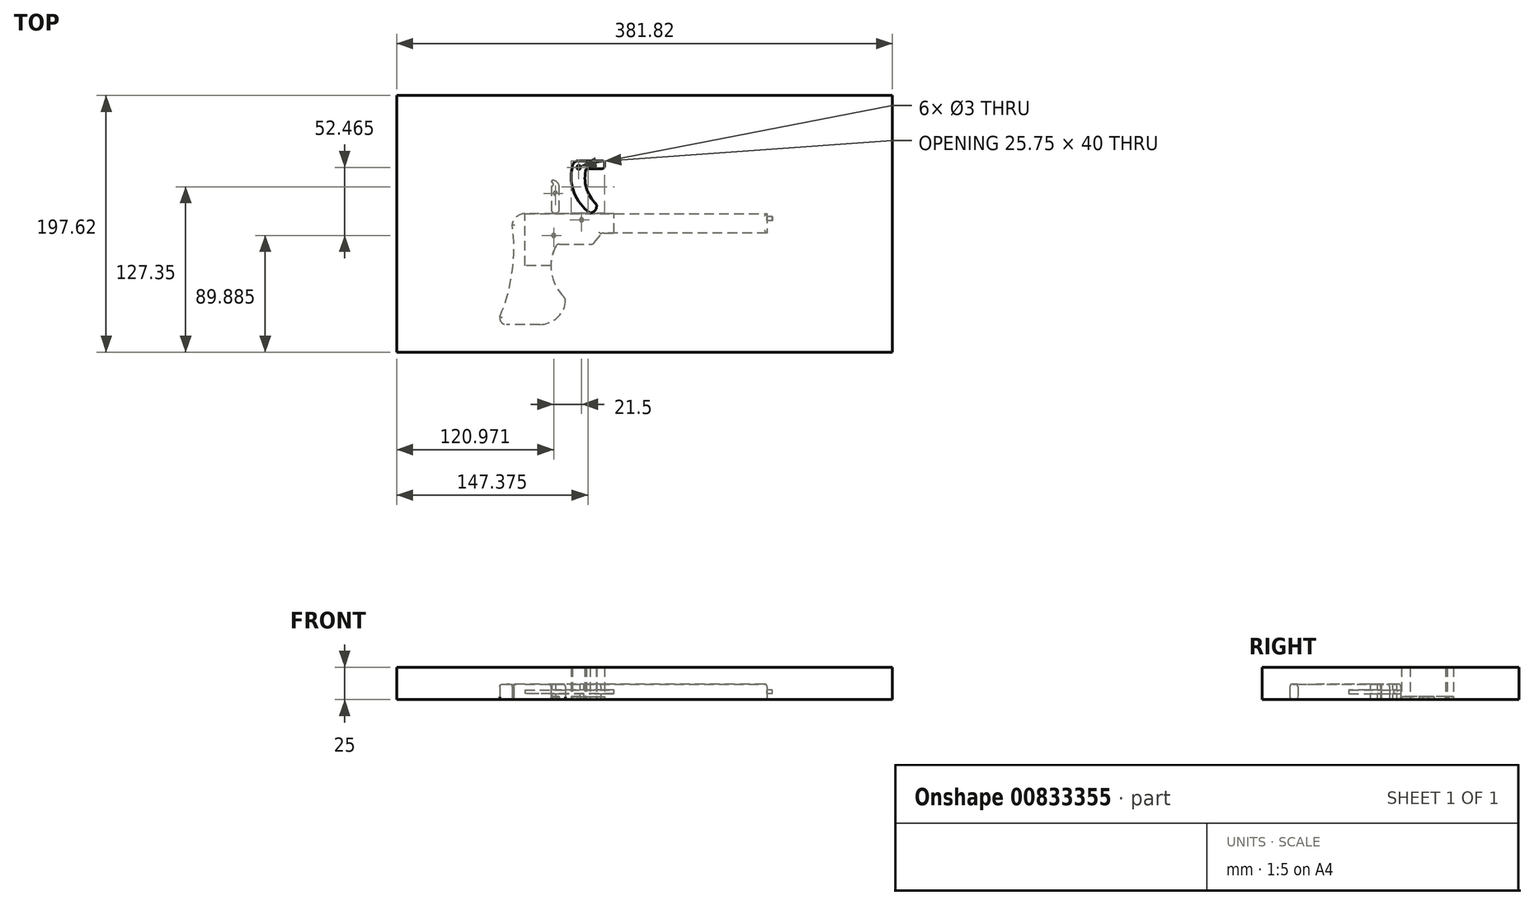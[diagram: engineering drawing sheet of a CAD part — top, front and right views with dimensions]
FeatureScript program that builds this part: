
annotation { "Feature Type Name" : "Feature", "Feature Type Description" : "" }
export const myFeature = defineFeature(function(context is Context, id is Id, definition is map)
    precondition{}
    {
        {
            var Q0;
            Q0=qCreatedBy(makeId("Top.planeOp"),FACE);
            var sketch = newSketch(context, id + "F0", { "sketchPlane" : qUnion([Q0])});
            skLineSegment(sketch, "E0", {"start": v(5, 40) * mm, "end": v(23, 40) * mm});
            skLineSegment(sketch, "E1", {"start": v(25, 38) * mm, "end": v(25, 36) * mm});
            skPoint(sketch, "E2.visualSharp", {"position": v(25, 40) * mm});
            skArc(sketch, "E2.filletArc", {"start": v(25, 38) * mm, "mid": v(24.41, 39.41) * mm, "end": v(23, 40) * mm});
            skPoint(sketch, "E3.visualSharp", {"position": v(25, 30) * mm});
            skPoint(sketch, "E4.visualSharp", {"position": v(0, 40) * mm});
            skArc(sketch, "E4.filletArc", {"start": v(5, 40) * mm, "mid": v(1.46, 38.54) * mm, "end": v(0, 35) * mm});
            skPoint(sketch, "E5.visualSharp", {"position": v(0, 0) * mm});
            skPoint(sketch, "E6.visualSharp", {"position": v(20.88, 0) * mm});
            skArc(sketch, "E6.filletArc", {"start": v(13.75, 0) * mm, "mid": v(17.85, 2.13) * mm, "end": v(18.45, 6.7) * mm});
            skArc(sketch, "E7", {"start": v(10.79, 34) * mm, "mid": v(10.83, 19.29) * mm, "end": v(18.45, 6.7) * mm});
            skArc(sketch, "E8", {"start": v(0, 35) * mm, "mid": v(1.46, 15.37) * mm, "end": v(13.75, 0) * mm});
            skCircle(sketch, "E9", {"center": v(5, 35) * mm, "radius": 1.5 * mm});
            skLineSegment(sketch, "E10.trimOffspring", {"start": v(10.79, 34) * mm, "end": v(23, 34) * mm});
            skPoint(sketch, "E11.visualSharp", {"position": v(25, 34) * mm});
            skArc(sketch, "E11.filletArc", {"start": v(23, 34) * mm, "mid": v(24.41, 34.59) * mm, "end": v(25, 36) * mm});
            skLineSegment(sketch, "E12.bottom", {"start": v(-135.25, 90.27) * mm, "end": v(246.57, 90.27) * mm});
            skLineSegment(sketch, "E12.top", {"start": v(-135.25, -107.35) * mm, "end": v(246.57, -107.35) * mm});
            skLineSegment(sketch, "E12.left", {"start": v(-135.25, 90.27) * mm, "end": v(-135.25, -107.35) * mm});
            skLineSegment(sketch, "E12.right", {"start": v(246.57, 90.27) * mm, "end": v(246.57, -107.35) * mm});
            skSolve(sketch);
        }
        {
            var Q0;
            Q0=makeQuery(id+"F0.imprint","IMPRINT",FACE,{"disambiguationData":[TD([[makeQuery(id+"F0.imprint","IMPRINT",EDGE,{"derivedFrom":sQuery(id+"F0.wireOp",EDGE,"E0")}),-1.0]])]});
            extrude(context, id + "F1", {"entities" : qUnion([Q0]), "depth" : 2.5 * mm, "offsetDistance" : 25 * mm});
        }
        {
            var Q0;
            Q0=qCreatedBy(makeId("Top.planeOp"),FACE);
            var sketch = newSketch(context, id + "F2", { "sketchPlane" : qUnion([Q0])});
            skLineSegment(sketch, "E13", {"start": v(-10, 2) * mm, "end": v(-10, 20) * mm});
            skLineSegment(sketch, "E14", {"start": v(-15, 25) * mm, "end": v(-15, 25) * mm});
            skLineSegment(sketch, "E15", {"start": v(-16, 24) * mm, "end": v(-16, 23.94) * mm});
            skLineSegment(sketch, "E16", {"start": v(-14, 0) * mm, "end": v(-12, 0) * mm});
            skLineSegment(sketch, "E17", {"start": v(-13, 0) * mm, "end": v(-13, 15) * mm});
            skCircle(sketch, "E18", {"center": v(-13, 15) * mm, "radius": 1.5 * mm});
            skArc(sketch, "E19", {"start": v(-16, 20.5) * mm, "mid": v(-14.51, 21.81) * mm, "end": v(-15.62, 23.45) * mm});
            skLineSegment(sketch, "E20.trimOffspring", {"start": v(-16, 20.5) * mm, "end": v(-16, 2) * mm});
            skPoint(sketch, "E21.visualSharp", {"position": v(-16, 25) * mm});
            skArc(sketch, "E21.filletArc", {"start": v(-15, 25) * mm, "mid": v(-15.7, 24.7) * mm, "end": v(-16, 24) * mm});
            skPoint(sketch, "E22.visualSharp", {"position": v(-16, 23.5) * mm});
            skArc(sketch, "E22.filletArc", {"start": v(-16, 23.94) * mm, "mid": v(-15.9, 23.63) * mm, "end": v(-15.62, 23.45) * mm});
            skPoint(sketch, "E23.visualSharp", {"position": v(-10, 25) * mm});
            skArc(sketch, "E23.filletArc", {"start": v(-10, 20) * mm, "mid": v(-11.46, 23.54) * mm, "end": v(-15, 25) * mm});
            skPoint(sketch, "E24.visualSharp", {"position": v(-10, 0) * mm});
            skArc(sketch, "E24.filletArc", {"start": v(-12, 0) * mm, "mid": v(-10.59, 0.59) * mm, "end": v(-10, 2) * mm});
            skPoint(sketch, "E25.visualSharp", {"position": v(-16, 0) * mm});
            skArc(sketch, "E25.filletArc", {"start": v(-16, 2) * mm, "mid": v(-15.41, 0.59) * mm, "end": v(-14, 0) * mm});
            skSolve(sketch);
        }
        {
            var Q0;
            Q0=makeQuery(id+"F2.imprint","IMPRINT",FACE,{"disambiguationData":[TD([[makeQuery(id+"F2.imprint","IMPRINT",EDGE,{"derivedFrom":sQuery(id+"F2.wireOp",EDGE,"E13")}),1.0]])]});
            extrude(context, id + "F3", {"entities" : qUnion([Q0]), "depth" : 2.5 * mm, "offsetDistance" : 25 * mm});
        }
        {
            var Q0;
            Q0=qCreatedBy(makeId("Top.planeOp"),FACE);
            var sketch = newSketch(context, id + "F4", { "sketchPlane" : qUnion([Q0])});
            skLineSegment(sketch, "E26", {"start": v(0, -0.6) * mm, "end": v(150, -0.6) * mm});
            skLineSegment(sketch, "E27", {"start": v(150, -0.6) * mm, "end": v(150, -15.6) * mm});
            skLineSegment(sketch, "E28", {"start": v(150, -15.6) * mm, "end": v(24.19, -15.6) * mm});
            skLineSegment(sketch, "E29", {"start": v(-25, -86) * mm, "end": v(-46.45, -86) * mm});
            skLineSegment(sketch, "E30", {"start": v(-36.37, -0.6) * mm, "end": v(0, -0.6) * mm});
            skPoint(sketch, "E31.visualSharp", {"position": v(-45, -0.6) * mm});
            skArc(sketch, "E31.filletArc", {"start": v(-36.37, -0.6) * mm, "mid": v(-42.9, -3.03) * mm, "end": v(-46.26, -9.15) * mm});
            skLineSegment(sketch, "E32", {"start": v(-46.45, -86) * mm, "end": v(-50.82, -86) * mm});
            skPoint(sketch, "E33.visualSharp", {"position": v(-56.45, -86) * mm});
            skArc(sketch, "E33.filletArc", {"start": v(-55.7, -79.93) * mm, "mid": v(-54.71, -84.14) * mm, "end": v(-50.82, -86) * mm});
            skPoint(sketch, "E34.visualSharp", {"position": v(-5, -86) * mm});
            skArc(sketch, "E34.filletArc", {"start": v(-25, -86) * mm, "mid": v(-11.86, -81.08) * mm, "end": v(-5.19, -68.73) * mm});
            skPoint(sketch, "E35.orphan", {"position": v(-5, -46) * mm});
            skArc(sketch, "E36", {"start": v(-12.68, -25.8) * mm, "mid": v(-15.98, -46.14) * mm, "end": v(-6.61, -64.5) * mm});
            skPoint(sketch, "E37.visualSharp", {"position": v(-5, -66) * mm});
            skArc(sketch, "E37.filletArc", {"start": v(-5.19, -68.73) * mm, "mid": v(-5.4, -66.45) * mm, "end": v(-6.61, -64.5) * mm});
            skArc(sketch, "E38", {"start": v(-55.7, -79.93) * mm, "mid": v(-46.19, -45.18) * mm, "end": v(-46.26, -9.15) * mm});
            skLineSegment(sketch, "E39", {"start": v(7.22, -3.96) * mm, "end": v(7.22, -5.46) * mm});
            skCircle(sketch, "E40", {"center": v(7.22, -5.46) * mm, "radius": 1.5 * mm});
            skPoint(sketch, "E41.visualSharp", {"position": v(23.03, -15.6) * mm});
            skArc(sketch, "E41.filletArc", {"start": v(24.19, -15.6) * mm, "mid": v(23.1, -15.8) * mm, "end": v(22.17, -16.37) * mm});
            skLineSegment(sketch, "E42", {"start": v(22.17, -16.37) * mm, "end": v(16.98, -23.01) * mm});
            skLineSegment(sketch, "E43", {"start": v(14.62, -24.17) * mm, "end": v(-10.02, -24.17) * mm});
            skPoint(sketch, "E44.visualSharp", {"position": v(-11.79, -24.17) * mm});
            skArc(sketch, "E44.filletArc", {"start": v(-10.02, -24.17) * mm, "mid": v(-11.58, -24.6) * mm, "end": v(-12.68, -25.8) * mm});
            skPoint(sketch, "E45.visualSharp", {"position": v(16.08, -24.17) * mm});
            skArc(sketch, "E45.filletArc", {"start": v(14.62, -24.17) * mm, "mid": v(15.93, -23.86) * mm, "end": v(16.98, -23.01) * mm});
            skCircle(sketch, "E46", {"center": v(-14.28, -17.46) * mm, "radius": 1.5 * mm});
            skSolve(sketch);
        }
        {
            var Q0;
            Q0=makeQuery(id+"F4.imprint","IMPRINT",FACE,{"disambiguationData":[TD([[makeQuery(id+"F4.imprint","IMPRINT",EDGE,{"derivedFrom":sQuery(id+"F4.wireOp",EDGE,"E26")}),-1.0]])]});
            extrude(context, id + "F5", {"entities" : qUnion([Q0]), "depth" : 12 * mm, "offsetDistance" : 25 * mm});
        }
        {
            var Q0;
            Q0=makeQuery(id+"F5.opExtrude","CAP_EDGE",EDGE,{"disambiguationData":[OSD([sQuery(id+"F4.wireOp",EDGE,"E26"),sQuery(id+"F4.wireOp",EDGE,"E30")])],"isStart":false});
            var Q1;
            Q1=makeQuery(id+"F5.opExtrude","CAP_EDGE",EDGE,{"disambiguationData":[OSD([sQuery(id+"F4.wireOp",EDGE,"E27")])],"isStart":false});
            var Q2;
            Q2=makeQuery(id+"F5.opExtrude","CAP_EDGE",EDGE,{"disambiguationData":[OSD([sQuery(id+"F4.wireOp",EDGE,"E28")])],"isStart":false});
            var Q3;
            Q3=makeQuery(id+"F5.opExtrude","CAP_EDGE",EDGE,{"disambiguationData":[OSD([sQuery(id+"F4.wireOp",EDGE,"bac6fea7-2e61-4f52-9ed3-d0ad31892a92.filletArc")])],"isStart":false});
            var Q4;
            Q4=makeQuery(id+"F5.opExtrude","CAP_EDGE",EDGE,{"disambiguationData":[OSD([sQuery(id+"F4.wireOp",EDGE,"E36")])],"isStart":false});
            var Q5;
            Q5=makeQuery(id+"F5.opExtrude","CAP_EDGE",EDGE,{"disambiguationData":[OSD([sQuery(id+"F4.wireOp",EDGE,"E37.filletArc")])],"isStart":false});
            var Q6;
            Q6=makeQuery(id+"F5.opExtrude","CAP_EDGE",EDGE,{"disambiguationData":[OSD([sQuery(id+"F4.wireOp",EDGE,"E34.filletArc")])],"isStart":false});
            var Q7;
            Q7=makeQuery(id+"F5.opExtrude","CAP_EDGE",EDGE,{"disambiguationData":[OSD([sQuery(id+"F4.wireOp",EDGE,"E29"),sQuery(id+"F4.wireOp",EDGE,"E32")])],"isStart":false});
            var Q8;
            Q8=makeQuery(id+"F5.opExtrude","CAP_EDGE",EDGE,{"disambiguationData":[OSD([sQuery(id+"F4.wireOp",EDGE,"E33.filletArc")])],"isStart":false});
            var Q9;
            Q9=makeQuery(id+"F5.opExtrude","CAP_EDGE",EDGE,{"disambiguationData":[OSD([sQuery(id+"F4.wireOp",EDGE,"E38")])],"isStart":false});
            var Q10;
            Q10=makeQuery(id+"F5.opExtrude","CAP_EDGE",EDGE,{"disambiguationData":[OSD([sQuery(id+"F4.wireOp",EDGE,"E31.filletArc")])],"isStart":false});
            var Q11;
            Q11=makeQuery(id+"F5.opExtrude","CAP_EDGE",EDGE,{"disambiguationData":[OSD([sQuery(id+"F4.wireOp",EDGE,"E29"),sQuery(id+"F4.wireOp",EDGE,"E32")])],"isStart":true});
            var Q12;
            Q12=makeQuery(id+"F5.opExtrude","CAP_EDGE",EDGE,{"disambiguationData":[OSD([sQuery(id+"F4.wireOp",EDGE,"E34.filletArc")])],"isStart":true});
            var Q13;
            Q13=makeQuery(id+"F5.opExtrude","CAP_EDGE",EDGE,{"disambiguationData":[OSD([sQuery(id+"F4.wireOp",EDGE,"E37.filletArc")])],"isStart":true});
            var Q14;
            Q14=makeQuery(id+"F5.opExtrude","CAP_EDGE",EDGE,{"disambiguationData":[OSD([sQuery(id+"F4.wireOp",EDGE,"E36")])],"isStart":true});
            var Q15;
            Q15=makeQuery(id+"F5.opExtrude","CAP_EDGE",EDGE,{"disambiguationData":[OSD([sQuery(id+"F4.wireOp",EDGE,"bac6fea7-2e61-4f52-9ed3-d0ad31892a92.filletArc")])],"isStart":true});
            var Q16;
            Q16=makeQuery(id+"F5.opExtrude","CAP_EDGE",EDGE,{"disambiguationData":[OSD([sQuery(id+"F4.wireOp",EDGE,"E28")])],"isStart":true});
            var Q17;
            Q17=makeQuery(id+"F5.opExtrude","CAP_EDGE",EDGE,{"disambiguationData":[OSD([sQuery(id+"F4.wireOp",EDGE,"E27")])],"isStart":true});
            var Q18;
            Q18=makeQuery(id+"F5.opExtrude","CAP_EDGE",EDGE,{"disambiguationData":[OSD([sQuery(id+"F4.wireOp",EDGE,"E26"),sQuery(id+"F4.wireOp",EDGE,"E30")])],"isStart":true});
            var Q19;
            Q19=makeQuery(id+"F5.opExtrude","CAP_EDGE",EDGE,{"disambiguationData":[OSD([sQuery(id+"F4.wireOp",EDGE,"E31.filletArc")])],"isStart":true});
            var Q20;
            Q20=makeQuery(id+"F5.opExtrude","CAP_EDGE",EDGE,{"disambiguationData":[OSD([sQuery(id+"F4.wireOp",EDGE,"E38")])],"isStart":true});
            var Q21;
            Q21=makeQuery(id+"F5.opExtrude","CAP_EDGE",EDGE,{"disambiguationData":[OSD([sQuery(id+"F4.wireOp",EDGE,"E33.filletArc")])],"isStart":true});
            fillet(context, id + "F6", {"entities" : qUnion([Q0, Q1, Q2, Q3, Q4, Q5, Q6, Q7, Q8, Q9, Q10, Q11, Q12, Q13, Q14, Q15, Q16, Q17, Q18, Q19, Q20, Q21]), "radius" : 2 * mm, "tangentPropagation" : true, "allowEdgeOverflow" : false});
        }
        {
            var Q0;
            Q0=makeQuery(id+"F5.opExtrude","SWEPT_FACE",FACE,{"disambiguationData":[OSD([sQuery(id+"F4.wireOp",EDGE,"E27")])]});
            var sketch = newSketch(context, id + "F7", { "sketchPlane" : qUnion([Q0])});
            skLineSegment(sketch, "E47", {"start": v(-0.6, 6) * mm, "end": v(-4.6, 6) * mm});
            skCircle(sketch, "E48", {"center": v(-4.6, 6) * mm, "radius": 1.5 * mm});
            skSolve(sketch);
        }
        {
            var Q0;
            Q0=makeQuery(id+"F7.imprint","IMPRINT",FACE,{"disambiguationData":[TD([[makeQuery(id+"F7.imprint","IMPRINT",EDGE,{"derivedFrom":sQuery(id+"F7.wireOp",EDGE,"E48")}),1.0]])]});
            var Q1;
            Q1=sQuery(id+"F7.wireOp",EDGE,"E48");
            extrude(context, id + "F8", {"entities" : qUnion([Q0]), "surfaceEntities" : qUnion([Q1]), "depth" : 4 * mm, "offsetDistance" : 25 * mm});
        }
        {
            var Q0;
            Q0=makeQuery(id+"F5.opExtrude","SWEPT_FACE",FACE,{"disambiguationData":[OSD([sQuery(id+"F4.wireOp",EDGE,"E26"),sQuery(id+"F4.wireOp",EDGE,"E30")])]});
            var sketch = newSketch(context, id + "F9", { "sketchPlane" : qUnion([Q0])});
            skLineSegment(sketch, "E49", {"start": v(-32.06, 6) * mm, "end": v(-32.06, 4.5) * mm});
            skLineSegment(sketch, "E50", {"start": v(-32.06, 4.5) * mm, "end": v(36.37, 4.5) * mm});
            skLineSegment(sketch, "E51", {"start": v(36.37, 4.5) * mm, "end": v(36.37, 6) * mm});
            skLineSegment(sketch, "E52", {"start": v(36.37, 6) * mm, "end": v(36.37, 7.5) * mm});
            skLineSegment(sketch, "E53", {"start": v(36.37, 7.5) * mm, "end": v(-32.06, 7.5) * mm});
            skLineSegment(sketch, "E54", {"start": v(-32.06, 7.5) * mm, "end": v(-32.06, 6) * mm});
            skSolve(sketch);
        }
        {
            var Q0;
            Q0=makeQuery(id+"F9.imprint","IMPRINT",FACE,{"disambiguationData":[TD([[makeQuery(id+"F9.imprint","IMPRINT",EDGE,{"derivedFrom":sQuery(id+"F9.wireOp",EDGE,"E49")}),1.0]])]});
            extrude(context, id + "F10", {"entities" : qUnion([Q0]), "operationType" : NewBodyOperationType.REMOVE, "oppositeDirection" : true, "depth" : 40 * mm, "offsetDistance" : 25 * mm});
        }
        {
            var Q0;
            Q0 = qSketchRegion(id + "F0", true);
            extrude(context, id + "F11", {"entities" : qUnion([Q0]), "depth" : 25 * mm, "offsetDistance" : 25 * mm});
        }
    });
